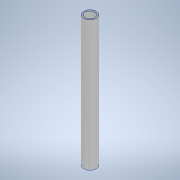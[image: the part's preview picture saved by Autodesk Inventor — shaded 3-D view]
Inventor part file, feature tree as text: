
AUTODESK INVENTOR PART (.ipt)
format: ipt  version: 2020.3 (Build 243373000, 373)  size: 96,768 bytes
history: native  units: mm
features: sketch x2, other x1, extrude x1, hole x1
ambient origin geometry x8: Origin, YZ Plane, XZ Plane, XY Plane, X Axis, Y Axis, Z Axis, Center Point
bodies: Body1 (feature_tree)
feature tree (5):
  other  "ソリッド1"
  extrude  "押し出し1"  Depth=4.0mm
  hole  "穴1"  [1 undecoded]
  sketch  "スケッチ1"
  sketch  "スケッチ2"
note: 1 required parameter value undecoded (feature->parameter linkage not recoverable at this tier; creation-order binding heuristic only, values carry confidence <= 0.55)
